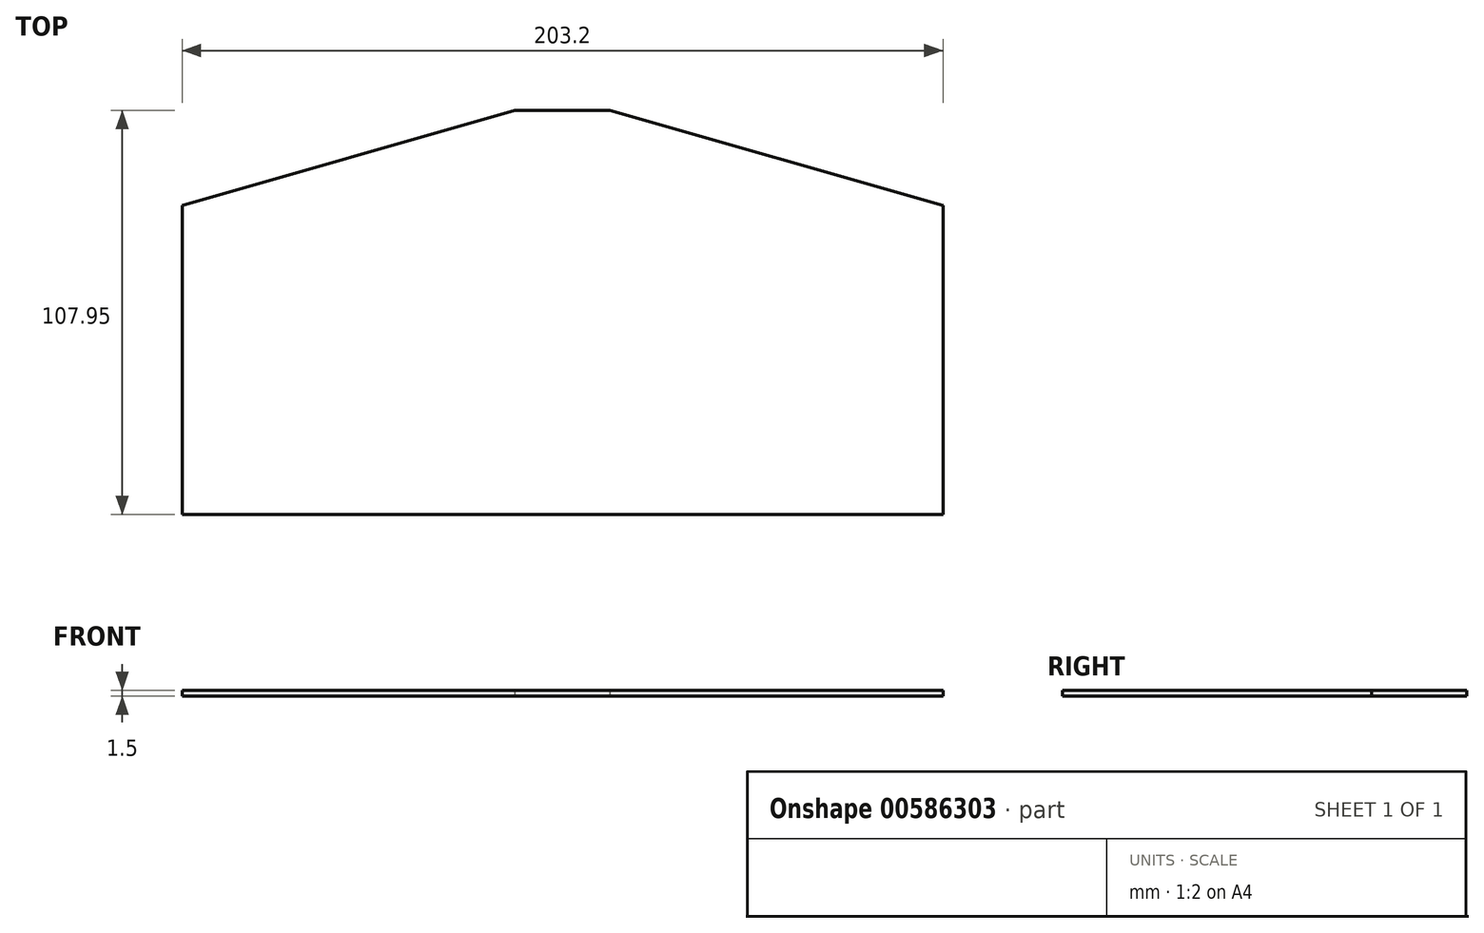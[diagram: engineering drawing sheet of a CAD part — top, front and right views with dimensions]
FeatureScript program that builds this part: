
annotation { "Feature Type Name" : "Feature", "Feature Type Description" : "" }
export const myFeature = defineFeature(function(context is Context, id is Id, definition is map)
    precondition{}
    {
        {
            var Q0;
            Q0=qCreatedBy(makeId("Top.planeOp"),FACE);
            var sketch = newSketch(context, id + "F0", { "sketchPlane" : qUnion([Q0])});
            skLineSegment(sketch, "E0", {"start": v(-106.67, 3.42) * mm, "end": v(-17.77, 28.82) * mm});
            skLineSegment(sketch, "E1", {"start": v(-17.77, 28.82) * mm, "end": v(7.63, 28.82) * mm});
            skLineSegment(sketch, "E2", {"start": v(7.63, 28.82) * mm, "end": v(96.53, 3.42) * mm});
            skLineSegment(sketch, "E3", {"start": v(96.53, 3.42) * mm, "end": v(96.53, -79.13) * mm});
            skLineSegment(sketch, "E4", {"start": v(96.53, -79.13) * mm, "end": v(-106.67, -79.13) * mm});
            skLineSegment(sketch, "E5", {"start": v(-106.67, 3.42) * mm, "end": v(-106.67, -79.13) * mm});
            skPoint(sketch, "E6.endSnap0", {"position": v(-5.07, -79.13) * mm});
            skPoint(sketch, "E6.end.orphan", {"position": v(-5.07, -79.13) * mm});
            skPoint(sketch, "E6.start.orphan", {"position": v(-5.07, 28.82) * mm});
            skSolve(sketch);
        }
        {
            var Q0;
            Q0=makeQuery(id+"F0.imprint","IMPRINT",FACE,{"disambiguationData":[TD([[makeQuery(id+"F0.imprint","IMPRINT",EDGE,{"derivedFrom":sQuery(id+"F0.wireOp",EDGE,"E0")}),-1.0]])]});
            extrude(context, id + "F1", {"entities" : qUnion([Q0]), "depth" : 1.5 * mm, "offsetDistance" : 25.4 * mm});
        }
    });
